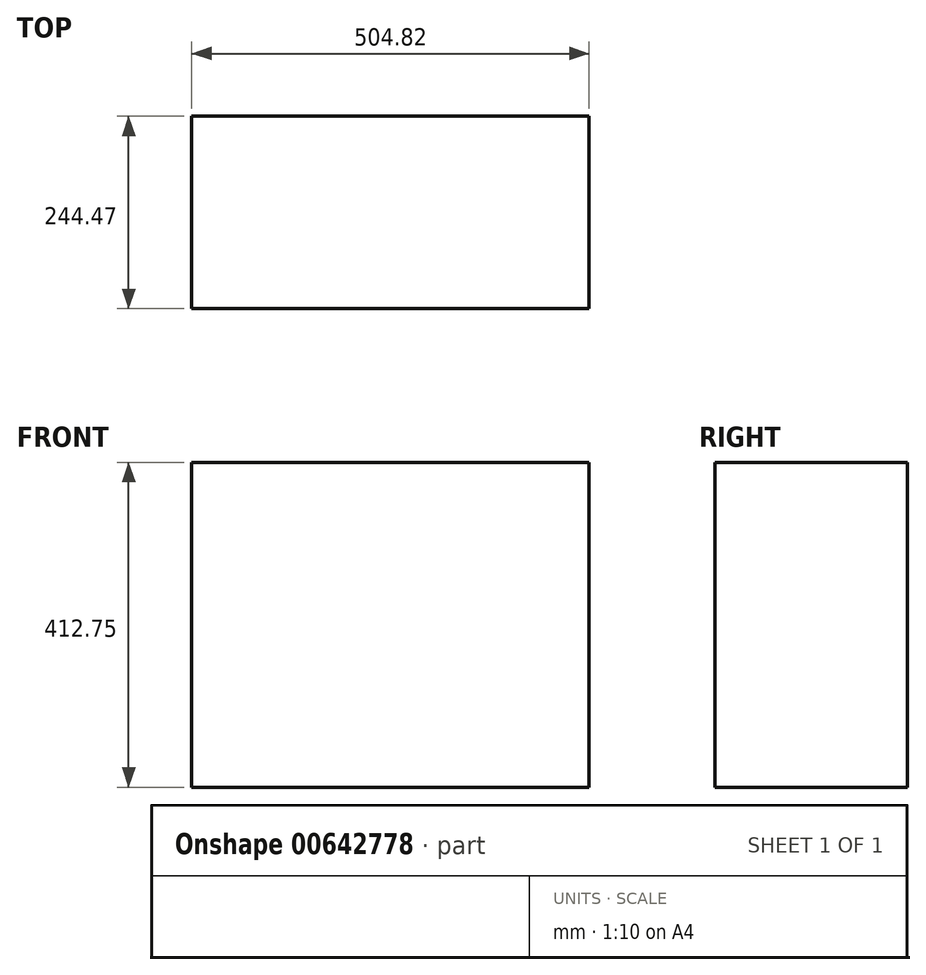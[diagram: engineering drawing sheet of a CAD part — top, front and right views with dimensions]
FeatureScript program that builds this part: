
annotation { "Feature Type Name" : "Feature", "Feature Type Description" : "" }
export const myFeature = defineFeature(function(context is Context, id is Id, definition is map)
    precondition{}
    {
        {
            var Q0;
            Q0=qCreatedBy(makeId("Front.planeOp"),FACE);
            var sketch = newSketch(context, id + "F0", { "sketchPlane" : qUnion([Q0])});
            skLineSegment(sketch, "E0.bottom", {"start": v(0, 0) * mm, "end": v(504.83, 0) * mm});
            skLineSegment(sketch, "E0.top", {"start": v(0, 412.75) * mm, "end": v(504.82, 412.75) * mm});
            skLineSegment(sketch, "E0.left", {"start": v(0, 0) * mm, "end": v(0, 412.75) * mm});
            skLineSegment(sketch, "E0.right", {"start": v(504.83, 0) * mm, "end": v(504.83, 412.75) * mm});
            skSolve(sketch);
        }
        {
            var Q0;
            Q0 = qSketchRegion(id + "F0", true);
            extrude(context, id + "F1", {"entities" : qUnion([Q0]), "depth" : 244.47 * mm, "offsetDistance" : 25.4 * mm});
        }
    });
